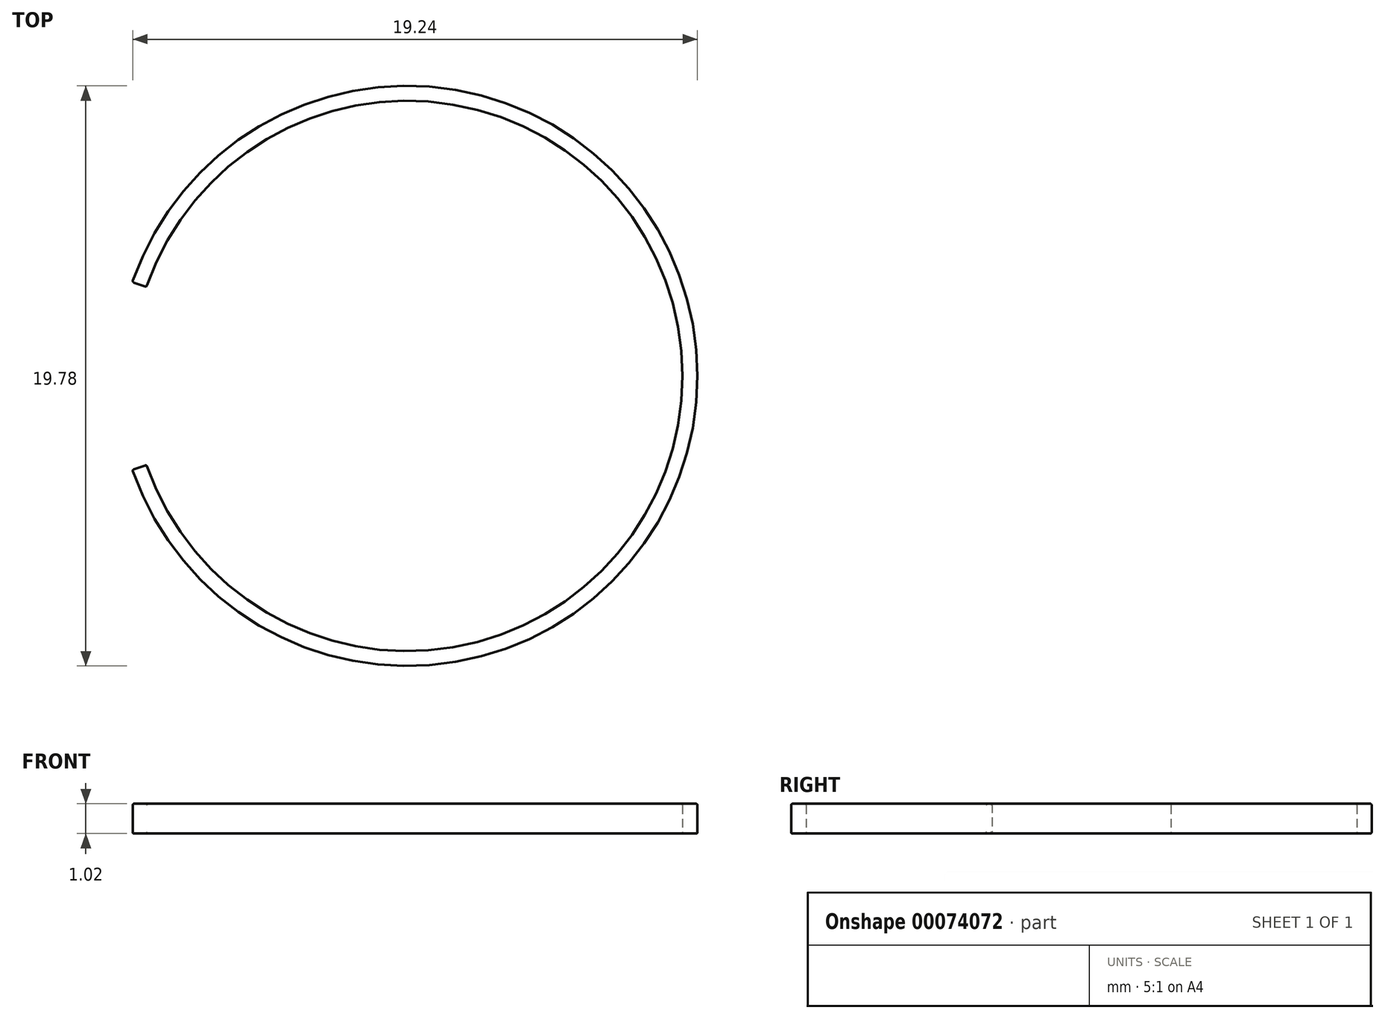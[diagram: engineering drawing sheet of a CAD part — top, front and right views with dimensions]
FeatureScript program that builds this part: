
annotation { "Feature Type Name" : "Feature", "Feature Type Description" : "" }
export const myFeature = defineFeature(function(context is Context, id is Id, definition is map)
    precondition{}
    {
        {
            var Q0;
            Q0=qCreatedBy(makeId("Top.planeOp"),FACE);
            var sketch = newSketch(context, id + "F0", { "sketchPlane" : qUnion([Q0])});
            skArc(sketch, "E0", {"start": v(-9.36, -3.2) * mm, "mid": v(9.9, 0) * mm, "end": v(-9.36, 3.2) * mm});
            skArc(sketch, "E1", {"start": v(-8.88, -3.04) * mm, "mid": v(9.39, 0) * mm, "end": v(-8.88, 3.04) * mm});
            skLineSegment(sketch, "E2", {"start": v(-8.88, -3.04) * mm, "end": v(-9.36, -3.2) * mm});
            skLineSegment(sketch, "E3", {"start": v(-9.36, -3.2) * mm, "end": v(-8.88, -3.04) * mm});
            skLineSegment(sketch, "E4", {"start": v(-9.36, 3.2) * mm, "end": v(-8.88, 3.04) * mm});
            skSolve(sketch);
        }
        {
            var Q0;
            Q0=makeQuery(id+"F0.imprint","IMPRINT",FACE,{"disambiguationData":[TD([[makeQuery(id+"F0.imprint","IMPRINT",EDGE,{"derivedFrom":sQuery(id+"F0.wireOp",EDGE,"E0")}),1.0]])]});
            extrude(context, id + "F1", {"entities" : qUnion([Q0]), "depth" : 1.02 * mm});
        }
        {
            var Q0;
            Q0=makeQuery(id+"F1.opExtrude","CAP_EDGE",EDGE,{"disambiguationData":[OSD([sQuery(id+"F0.wireOp",EDGE,"E1")])],"isStart":false});
            var Q1;
            Q1=makeQuery(id+"F1.opExtrude","CAP_EDGE",EDGE,{"disambiguationData":[OSD([sQuery(id+"F0.wireOp",EDGE,"E0")])],"isStart":false});
            var Q2;
            Q2=makeQuery(id+"F1.opExtrude","CAP_EDGE",EDGE,{"disambiguationData":[OSD([sQuery(id+"F0.wireOp",EDGE,"E0")])],"isStart":true});
            var Q3;
            Q3=makeQuery(id+"F1.opExtrude","CAP_EDGE",EDGE,{"disambiguationData":[OSD([sQuery(id+"F0.wireOp",EDGE,"E1")])],"isStart":true});
            var Q4;
            Q4=makeQuery(id+"F1.opExtrude","SWEPT_EDGE",EDGE,{"disambiguationData":[OSD([sQuery(id+"F0.wireOp",EDGE,"E1"),sQuery(id+"F0.wireOp",EDGE,"E3")])]});
            var Q5;
            Q5=makeQuery(id+"F1.opExtrude","SWEPT_EDGE",EDGE,{"disambiguationData":[OSD([sQuery(id+"F0.wireOp",EDGE,"E1"),sQuery(id+"F0.wireOp",EDGE,"E4")])]});
            var Q6;
            Q6=makeQuery(id+"F1.opExtrude","SWEPT_EDGE",EDGE,{"disambiguationData":[OSD([sQuery(id+"F0.wireOp",EDGE,"E0"),sQuery(id+"F0.wireOp",EDGE,"E4")])]});
            var Q7;
            Q7=makeQuery(id+"F1.opExtrude","CAP_EDGE",EDGE,{"disambiguationData":[OSD([sQuery(id+"F0.wireOp",EDGE,"E4")])],"isStart":true});
            var Q8;
            Q8=makeQuery(id+"F1.opExtrude","CAP_EDGE",EDGE,{"disambiguationData":[OSD([sQuery(id+"F0.wireOp",EDGE,"E4")])],"isStart":false});
            var Q9;
            Q9=makeQuery(id+"F1.opExtrude","CAP_EDGE",EDGE,{"disambiguationData":[OSD([sQuery(id+"F0.wireOp",EDGE,"E3")])],"isStart":true});
            var Q10;
            Q10=makeQuery(id+"F1.opExtrude","SWEPT_EDGE",EDGE,{"disambiguationData":[OSD([sQuery(id+"F0.wireOp",EDGE,"E0"),sQuery(id+"F0.wireOp",EDGE,"E3")])]});
            var Q11;
            Q11=makeQuery(id+"F1.opExtrude","CAP_EDGE",EDGE,{"disambiguationData":[OSD([sQuery(id+"F0.wireOp",EDGE,"E3")])],"isStart":false});
            fillet(context, id + "F2", {"entities" : qUnion([Q0, Q1, Q2, Q3, Q4, Q5, Q6, Q7, Q8, Q9, Q10, Q11]), "radius" : 0.05 * mm, "tangentPropagation" : true, "allowEdgeOverflow" : false});
        }
    });
